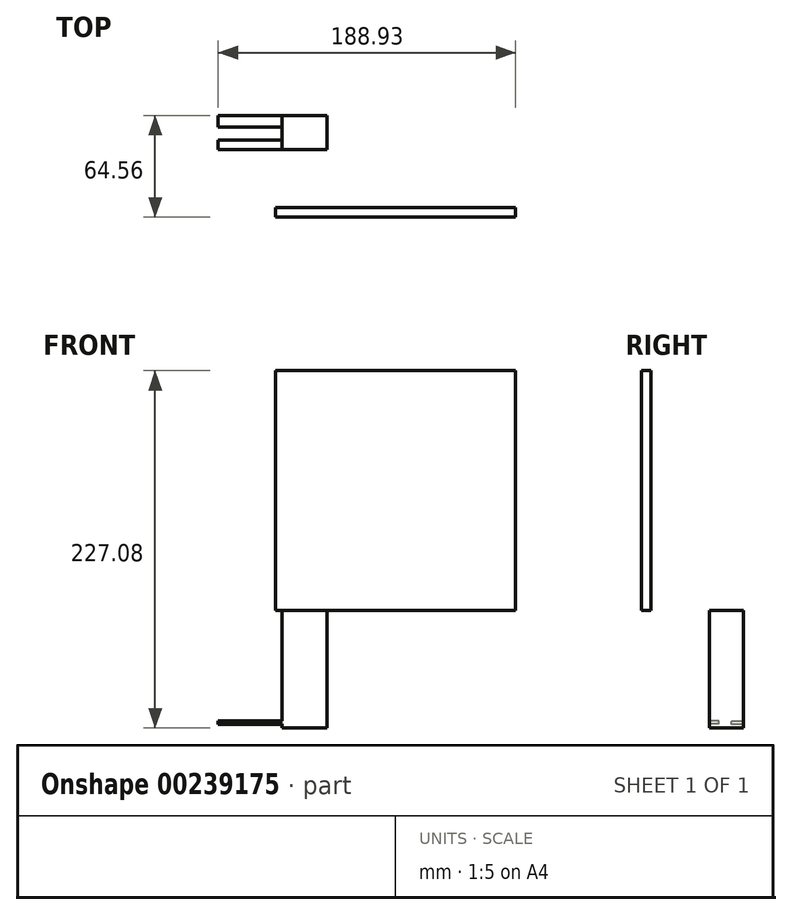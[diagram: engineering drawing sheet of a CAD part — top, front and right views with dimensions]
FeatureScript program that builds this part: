
annotation { "Feature Type Name" : "Feature", "Feature Type Description" : "" }
export const myFeature = defineFeature(function(context is Context, id is Id, definition is map)
    precondition{}
    {
        {
            assignVariable(context, id + "F0", {"name" : "E", "anyValue" : 6});
        }
        {
            var Q0;
            Q0=qCreatedBy(makeId("Front.planeOp"),FACE);
            var sketch = newSketch(context, id + "F1", { "sketchPlane" : qUnion([Q0])});
            skLineSegment(sketch, "E0.bottom", {"start": v(76.2, 76.2) * mm, "end": v(-76.2, 76.2) * mm});
            skLineSegment(sketch, "E0.top", {"start": v(76.2, -76.2) * mm, "end": v(-76.2, -76.2) * mm});
            skLineSegment(sketch, "E0.left", {"start": v(76.2, 76.2) * mm, "end": v(76.2, -76.2) * mm});
            skLineSegment(sketch, "E0.right", {"start": v(-76.2, 76.2) * mm, "end": v(-76.2, -76.2) * mm});
            skPoint(sketch, "E0.middle", {"position": v(0, 0) * mm});
            skSolve(sketch);
        }
        {
            var Q0;
            Q0 = qSketchRegion(id + "F1", true);
            extrude(context, id + "F2", {"entities" : qUnion([Q0]), "endBound" : BoundingType.SYMMETRIC, "depth" : (getVariable(context, 'E')) * mm});
        }
        {
            var Q0;
            Q0=makeQuery(id+"F2.opExtrude","SWEPT_FACE",FACE,{"disambiguationData":[OSD([sQuery(id+"F1.wireOp",EDGE,"E0.bottom")])]});
            var sketch = newSketch(context, id + "F3", { "sketchPlane" : qUnion([Q0])});
            skLineSegment(sketch, "E1.bottom", {"start": v(-43.47, 39.96) * mm, "end": v(-72.1, 39.96) * mm});
            skLineSegment(sketch, "E1.top", {"start": v(-43.47, 61.56) * mm, "end": v(-72.1, 61.56) * mm});
            skLineSegment(sketch, "E1.left", {"start": v(-43.47, 39.96) * mm, "end": v(-43.47, 61.56) * mm});
            skLineSegment(sketch, "E1.right", {"start": v(-72.1, 39.96) * mm, "end": v(-72.1, 61.56) * mm});
            skPoint(sketch, "E1.middle", {"position": v(-57.78, 50.76) * mm});
            skSolve(sketch);
        }
        {
            var Q0;
            Q0 = qSketchRegion(id + "F3", true);
            var Q1;
            Q1=makeQuery(id+"F2.opExtrude","SWEPT_FACE",FACE,{"disambiguationData":[OSD([sQuery(id+"F1.wireOp",EDGE,"E0.top")])]});
            extrude(context, id + "F4", {"entities" : qUnion([Q0, Q1]), "operationType" : NewBodyOperationType.REMOVE, "oppositeDirection" : true, "depth" : 81.28 * mm});
        }
        {
            var Q0;
            Q0=makeQuery(id+"F2.opExtrude","SWEPT_FACE",FACE,{"disambiguationData":[OSD([sQuery(id+"F1.wireOp",EDGE,"E0.top")])]});
            var sketch = newSketch(context, id + "F5", { "sketchPlane" : qUnion([Q0])});
            skLineSegment(sketch, "E2.0", {"start": v(-43.47, -61.56) * mm, "end": v(-72.1, -61.56) * mm});
            skLineSegment(sketch, "E3.0", {"start": v(-43.47, -39.96) * mm, "end": v(-43.47, -61.56) * mm});
            skPoint(sketch, "E4.0", {"position": v(-57.78, -39.96) * mm});
            skLineSegment(sketch, "E5.0", {"start": v(-43.47, -39.96) * mm, "end": v(-72.1, -39.96) * mm});
            skLineSegment(sketch, "E6.0", {"start": v(-72.1, -39.96) * mm, "end": v(-72.1, -61.56) * mm});
            skSolve(sketch);
        }
        {
            var Q0;
            Q0 = qSketchRegion(id + "F5", true);
            extrude(context, id + "F6", {"entities" : qUnion([Q0]), "operationType" : NewBodyOperationType.ADD, "depth" : 74.68 * mm});
        }
        {
            var Q0;
            Q0=makeQuery(id+"F6.opExtrude","SWEPT_FACE",FACE,{"disambiguationData":[OSD([sQuery(id+"F5.wireOp",EDGE,"E6.0")])]});
            var sketch = newSketch(context, id + "F7", { "sketchPlane" : qUnion([Q0])});
            skLineSegment(sketch, "E7.bottom", {"start": v(-61.56, -148.48) * mm, "end": v(-54.06, -148.48) * mm});
            skLineSegment(sketch, "E7.top", {"start": v(-61.56, -146.76) * mm, "end": v(-54.06, -146.76) * mm});
            skLineSegment(sketch, "E7.left", {"start": v(-61.56, -148.48) * mm, "end": v(-61.56, -146.76) * mm});
            skLineSegment(sketch, "E7.right", {"start": v(-54.06, -148.48) * mm, "end": v(-54.06, -146.76) * mm});
            skLineSegment(sketch, "E8.bottom", {"start": v(-46.04, -148.19) * mm, "end": v(-39.96, -148.19) * mm});
            skLineSegment(sketch, "E8.top", {"start": v(-46.04, -146.46) * mm, "end": v(-39.96, -146.46) * mm});
            skLineSegment(sketch, "E8.left", {"start": v(-46.04, -148.19) * mm, "end": v(-46.04, -146.46) * mm});
            skLineSegment(sketch, "E8.right", {"start": v(-39.96, -148.19) * mm, "end": v(-39.96, -146.46) * mm});
            skSolve(sketch);
        }
        {
            var Q0;
            Q0 = qSketchRegion(id + "F7", true);
            extrude(context, id + "F8", {"entities" : qUnion([Q0]), "operationType" : NewBodyOperationType.ADD, "depth" : 40.64 * mm});
        }
    });
